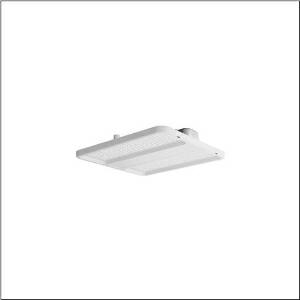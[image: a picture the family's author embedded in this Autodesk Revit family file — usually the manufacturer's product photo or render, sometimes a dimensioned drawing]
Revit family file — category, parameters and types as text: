
# Revit family: highbay_11_midi_51hn12da4hda
name_source: partatom
category: Lighting Fixtures
units: mm (PartAtom-declared; Revit-internal decimal feet)

## family parameters
Cut with Voids When Loaded = No
Host = Face
Light Source = No
Part Type = Normal
Room Calculation Point = No
Round Connector Dimension = Use Diameter
Shared = No

## types (1)
- --- (1 x LED, 2890 lm, 14.5 W, 4000K)
    Apparent Load = 15 VA
    CIE Flux Codes = 87 98 100 100 100
    Color Rendering = 80
    Color Temperature = 4000K
    Default Elevation = 1800 mm
    Description = high bay luminaire Highbay 11 midi; direct symmetric wide distribution, light control with lens of PMMA; UGR ≤ 22 (X = 4H | Y = 8H | S = 0.25H | reflection values 70/50/20); luminous flux: 18.500lm; light colour: 840, colour temperature: 4000K, MacAdam ≤ 2 SDCM (initial), colour rendering: CRI > 80; luminous efficacy: 201,5lm/W; rated service life: 100.000h (L95/B50) at AT= 25°C; control: DALI 2; housing frame of high-performance plastic PA6, matt traffic white (RAL 9016); cover of PMMA; dimension (LxWxH): 474 x 442 x 72mm; luminaire connection: terminal, 5-pole, max. 2.5mm² (cable entry for one cable, Ø 8.5..16mm); mains connection: 230..240V, AC/DC 0/50..60Hz; connected load: 91,8W; protection rating (complete): IP66; insulation class (complete): insulation class I (protective earthing); protection symbol: D; impact resistance: IK08; halogen-free wiring; for central battery installations according to DIN EN 60598-2-22; corresponds to IFS (International Featured Standards) requirements for safety and quality in the food industry; LABS conformity tested according to VDMA 24364:2018-05; certification: CE, ENEC, VDE, UKCA; permissible operating ambient temperature: -40..+60°C (reducing of maximum allowable ambient temperature of 5°C with ceiling mounting); packaging unit: 1 piece; (delivery without accessories; please order mounting accessories separately)
    Height = 72 mm  [stored 0.23622 ft]
    Lamp = 1 x LED
    Lamp Light Flux = 2890 lm
    Lamp Power = 14.5 W
    Lamp count = 1
    Length = 474 mm
    Luminous efficacy = 199 lm/W
    Manufacturer = Siteco
    ModVariant = No
    Model = 51HN12DA4HDA
    Mounting Place = Ceiling
    Mounting Type = Pendant
    Number of Poles = 1
    OnlyDefault = Yes
    Power Factor = 1
    Product Name = Highbay 11 midi
    Product group = high bay luminaire
    ProductGroupID = 901
    Protection Class = Protection class I
    Protection Degree = IP 66
    RLX_Detail_Level = 1
    RLX_Emergency_Light_Flux = 0 lm
    RLX_Emergency_Type = 0
    RLX_Emergency_Type_DB = No
    RlxData = <blob elided: 16677 chars, md5=de30d61f>
    Socket = socket
    Standby Power = 0 W
    System Light Flux = 2890 lm
    System Power = 15 W
    Type Comments = : DC mode (central or group accumulator) initial emergency light level
    Type Image = l_1363240.jpg
    URL = http://relux.com
    VarID = @adj_005183
    Voltage = 0 V
    Weight = 0.00 kg
    Width = 442 mm

note: [stored X ft] marks values corroborated as IEEE doubles in the binary element streams (Revit-internal decimal feet)

## geometry (parser evidence)
native form markers: Blend x4, Sweep x10
no freeform markers — native parametric forms only
